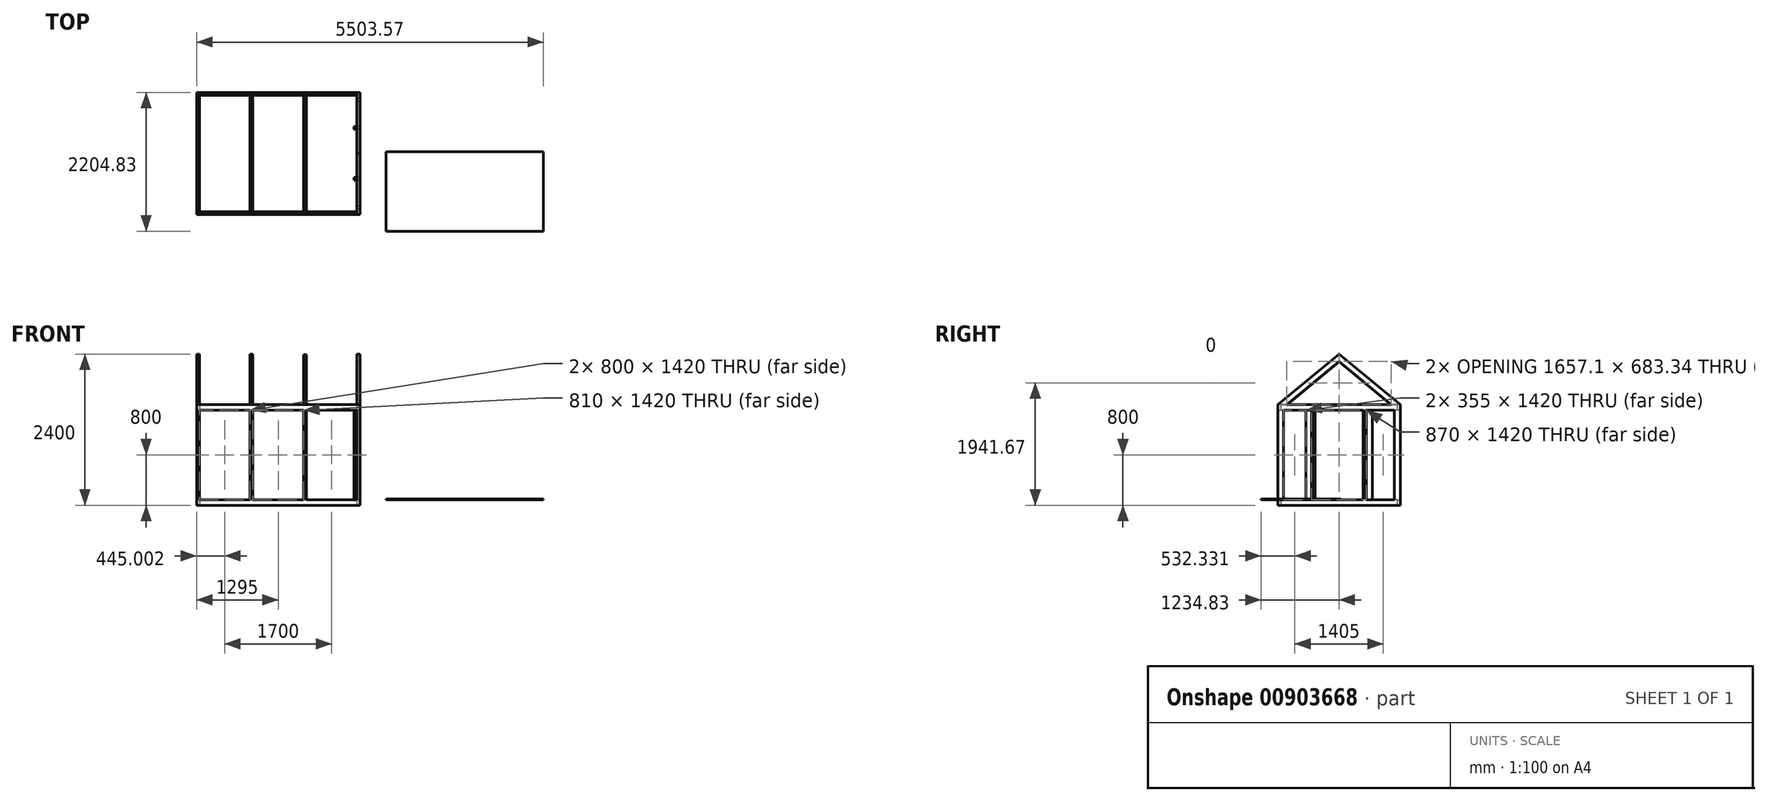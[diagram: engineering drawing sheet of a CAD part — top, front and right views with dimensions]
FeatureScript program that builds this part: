
annotation { "Feature Type Name" : "Feature", "Feature Type Description" : "" }
export const myFeature = defineFeature(function(context is Context, id is Id, definition is map)
    precondition{}
    {
        {
            var Q0;
            Q0=qCreatedBy(makeId("Top.planeOp"),FACE);
            var sketch = newSketch(context, id + "F0", { "sketchPlane" : qUnion([Q0])});
            skLineSegment(sketch, "E0.bottom", {"start": v(-727.48, 1617.18) * mm, "end": v(1862.52, 1617.18) * mm});
            skLineSegment(sketch, "E0.top", {"start": v(-727.48, -322.82) * mm, "end": v(1862.52, -322.82) * mm});
            skLineSegment(sketch, "E0.left", {"start": v(-727.48, 1617.18) * mm, "end": v(-727.48, -322.82) * mm});
            skLineSegment(sketch, "E0.right", {"start": v(1862.52, 1617.18) * mm, "end": v(1862.52, -322.82) * mm});
            skLineSegment(sketch, "E1.bottom", {"start": v(-682.48, 1572.18) * mm, "end": v(1817.52, 1572.18) * mm});
            skLineSegment(sketch, "E1.top", {"start": v(-682.48, -277.82) * mm, "end": v(1817.52, -277.82) * mm});
            skLineSegment(sketch, "E1.left", {"start": v(-682.48, 1572.18) * mm, "end": v(-682.48, -277.82) * mm});
            skLineSegment(sketch, "E1.right", {"start": v(1817.52, 1572.18) * mm, "end": v(1817.52, -277.82) * mm});
            skSolve(sketch);
        }
        {
            var Q0;
            Q0 = qSketchRegion(id + "F0", true);
            extrude(context, id + "F1", {"entities" : qUnion([Q0]), "depth" : 90 * mm, "offsetDistance" : 25 * mm});
        }
        {
            var Q0;
            Q0=makeQuery(id+"F1.opExtrude","CAP_FACE",FACE,{"disambiguationData":[OSD([sQuery(id+"F0.wireOp",EDGE,"E0.bottom"),sQuery(id+"F0.wireOp",EDGE,"E0.top"),sQuery(id+"F0.wireOp",EDGE,"E0.left"),sQuery(id+"F0.wireOp",EDGE,"E0.right"),sQuery(id+"F0.wireOp",EDGE,"E1.bottom"),sQuery(id+"F0.wireOp",EDGE,"E1.top"),sQuery(id+"F0.wireOp",EDGE,"E1.left"),sQuery(id+"F0.wireOp",EDGE,"E1.right")])],"isStart":false});
            var sketch = newSketch(context, id + "F2", { "sketchPlane" : qUnion([Q0])});
            skLineSegment(sketch, "E2.bottom", {"start": v(-727.48, -322.82) * mm, "end": v(-682.48, -322.82) * mm});
            skLineSegment(sketch, "E2.top", {"start": v(-727.48, -232.82) * mm, "end": v(-682.48, -232.82) * mm});
            skLineSegment(sketch, "E2.left", {"start": v(-727.48, -322.82) * mm, "end": v(-727.48, -232.82) * mm});
            skLineSegment(sketch, "E2.right", {"start": v(-682.48, -322.82) * mm, "end": v(-682.48, -232.82) * mm});
            skLineSegment(sketch, "E3.bottom", {"start": v(-727.48, 1617.18) * mm, "end": v(-682.48, 1617.18) * mm});
            skLineSegment(sketch, "E3.top", {"start": v(-727.48, 1527.18) * mm, "end": v(-682.48, 1527.18) * mm});
            skLineSegment(sketch, "E3.left", {"start": v(-727.48, 1617.18) * mm, "end": v(-727.48, 1527.18) * mm});
            skLineSegment(sketch, "E3.right", {"start": v(-682.48, 1617.18) * mm, "end": v(-682.48, 1527.18) * mm});
            skLineSegment(sketch, "E4.bottom", {"start": v(1862.52, 1617.18) * mm, "end": v(1817.52, 1617.18) * mm});
            skLineSegment(sketch, "E4.top", {"start": v(1862.52, 1527.18) * mm, "end": v(1817.52, 1527.18) * mm});
            skLineSegment(sketch, "E4.left", {"start": v(1862.52, 1617.18) * mm, "end": v(1862.52, 1527.18) * mm});
            skLineSegment(sketch, "E4.right", {"start": v(1817.52, 1617.18) * mm, "end": v(1817.52, 1527.18) * mm});
            skLineSegment(sketch, "E5.bottom", {"start": v(1862.52, -322.82) * mm, "end": v(1817.52, -322.82) * mm});
            skLineSegment(sketch, "E5.top", {"start": v(1862.52, -232.82) * mm, "end": v(1817.52, -232.82) * mm});
            skLineSegment(sketch, "E5.left", {"start": v(1862.52, -322.82) * mm, "end": v(1862.52, -232.82) * mm});
            skLineSegment(sketch, "E5.right", {"start": v(1817.52, -322.82) * mm, "end": v(1817.52, -232.82) * mm});
            skLineSegment(sketch, "E6.bottom", {"start": v(117.52, -232.82) * mm, "end": v(162.52, -232.82) * mm});
            skLineSegment(sketch, "E6.top", {"start": v(117.52, -322.82) * mm, "end": v(162.52, -322.82) * mm});
            skLineSegment(sketch, "E6.left", {"start": v(117.52, -232.82) * mm, "end": v(117.52, -322.82) * mm});
            skLineSegment(sketch, "E6.right", {"start": v(162.52, -232.82) * mm, "end": v(162.52, -322.82) * mm});
            skLineSegment(sketch, "E7.bottom", {"start": v(972.52, -232.82) * mm, "end": v(1017.52, -232.82) * mm});
            skLineSegment(sketch, "E7.top", {"start": v(972.52, -322.82) * mm, "end": v(1017.52, -322.82) * mm});
            skLineSegment(sketch, "E7.left", {"start": v(972.52, -232.82) * mm, "end": v(972.52, -322.82) * mm});
            skLineSegment(sketch, "E7.right", {"start": v(1017.52, -232.82) * mm, "end": v(1017.52, -322.82) * mm});
            skLineSegment(sketch, "E8.bottom", {"start": v(117.52, 1617.18) * mm, "end": v(162.52, 1617.18) * mm});
            skLineSegment(sketch, "E8.top", {"start": v(117.52, 1527.18) * mm, "end": v(162.52, 1527.18) * mm});
            skLineSegment(sketch, "E8.left", {"start": v(117.52, 1617.18) * mm, "end": v(117.52, 1527.18) * mm});
            skLineSegment(sketch, "E8.right", {"start": v(162.52, 1617.18) * mm, "end": v(162.52, 1527.18) * mm});
            skLineSegment(sketch, "E9.bottom", {"start": v(1017.52, 1527.18) * mm, "end": v(972.52, 1527.18) * mm});
            skLineSegment(sketch, "E9.top", {"start": v(1017.52, 1617.18) * mm, "end": v(972.52, 1617.18) * mm});
            skLineSegment(sketch, "E9.left", {"start": v(1017.52, 1527.18) * mm, "end": v(1017.52, 1617.18) * mm});
            skLineSegment(sketch, "E9.right", {"start": v(972.52, 1527.18) * mm, "end": v(972.52, 1617.18) * mm});
            skLineSegment(sketch, "E10.bottom", {"start": v(-727.48, 1172.18) * mm, "end": v(-682.48, 1172.18) * mm});
            skLineSegment(sketch, "E10.top", {"start": v(-727.48, 1082.18) * mm, "end": v(-682.48, 1082.18) * mm});
            skLineSegment(sketch, "E10.left", {"start": v(-727.48, 1172.18) * mm, "end": v(-727.48, 1082.18) * mm});
            skLineSegment(sketch, "E10.right", {"start": v(-682.48, 1172.18) * mm, "end": v(-682.48, 1082.18) * mm});
            skLineSegment(sketch, "E11.bottom", {"start": v(-727.48, 212.18) * mm, "end": v(-682.48, 212.18) * mm});
            skLineSegment(sketch, "E11.top", {"start": v(-727.48, 122.18) * mm, "end": v(-682.48, 122.18) * mm});
            skLineSegment(sketch, "E11.left", {"start": v(-727.48, 212.18) * mm, "end": v(-727.48, 122.18) * mm});
            skLineSegment(sketch, "E11.right", {"start": v(-682.48, 212.18) * mm, "end": v(-682.48, 122.18) * mm});
            skLineSegment(sketch, "E12.bottom", {"start": v(1862.52, 1072.18) * mm, "end": v(1772.52, 1072.18) * mm});
            skLineSegment(sketch, "E12.top", {"start": v(1862.52, 1027.18) * mm, "end": v(1772.52, 1027.18) * mm});
            skLineSegment(sketch, "E12.left", {"start": v(1862.52, 1072.18) * mm, "end": v(1862.52, 1027.18) * mm});
            skLineSegment(sketch, "E12.right", {"start": v(1772.52, 1072.18) * mm, "end": v(1772.52, 1027.18) * mm});
            skLineSegment(sketch, "E13.bottom", {"start": v(1862.52, 267.18) * mm, "end": v(1772.52, 267.18) * mm});
            skLineSegment(sketch, "E13.top", {"start": v(1862.52, 222.18) * mm, "end": v(1772.52, 222.18) * mm});
            skLineSegment(sketch, "E13.left", {"start": v(1862.52, 267.18) * mm, "end": v(1862.52, 222.18) * mm});
            skLineSegment(sketch, "E13.right", {"start": v(1772.52, 267.18) * mm, "end": v(1772.52, 222.18) * mm});
            skSolve(sketch);
        }
        {
            var Q0;
            {var subQ0=sQuery(id+"F2.wireOp",EDGE,"E10.left");Q0=makeQuery(id+"F2.imprint","IMPRINT",FACE,{"disambiguationData":[TD([[makeQuery(id+"F2.imprint","IMPRINT",EDGE,{"derivedFrom":subQ0}),1.0]])]});}
            var Q1;
            {var subQ0=sQuery(id+"F2.wireOp",EDGE,"E10.right");Q1=makeQuery(id+"F2.imprint","IMPRINT",FACE,{"disambiguationData":[TD([[makeQuery(id+"F2.imprint","IMPRINT",EDGE,{"derivedFrom":subQ0}),-1.0]])]});}
            var Q2;
            {var subQ0=sQuery(id+"F2.wireOp",EDGE,"E11.left");Q2=makeQuery(id+"F2.imprint","IMPRINT",FACE,{"disambiguationData":[TD([[makeQuery(id+"F2.imprint","IMPRINT",EDGE,{"derivedFrom":subQ0}),1.0]])]});}
            var Q3;
            {var subQ0=sQuery(id+"F2.wireOp",EDGE,"E11.right");Q3=makeQuery(id+"F2.imprint","IMPRINT",FACE,{"disambiguationData":[TD([[makeQuery(id+"F2.imprint","IMPRINT",EDGE,{"derivedFrom":subQ0}),-1.0]])]});}
            var Q4;
            {var subQ2=sQuery(id+"F2.wireOp",EDGE,"E2.bottom");Q4=makeQuery(id+"F2.imprint","IMPRINT",FACE,{"disambiguationData":[TD([[makeQuery(id+"F2.imprint","IMPRINT",EDGE,{"derivedFrom":subQ2}),1.0]])]});}
            var Q5;
            {var subQ0=sQuery(id+"F2.wireOp",EDGE,"E6.bottom");Q5=makeQuery(id+"F2.imprint","IMPRINT",FACE,{"disambiguationData":[TD([[makeQuery(id+"F2.imprint","IMPRINT",EDGE,{"derivedFrom":subQ0}),-1.0]])]});}
            var Q6;
            {var subQ0=sQuery(id+"F2.wireOp",EDGE,"E6.top");Q6=makeQuery(id+"F2.imprint","IMPRINT",FACE,{"disambiguationData":[TD([[makeQuery(id+"F2.imprint","IMPRINT",EDGE,{"derivedFrom":subQ0}),1.0]])]});}
            var Q7;
            {var subQ0=sQuery(id+"F2.wireOp",EDGE,"E7.bottom");Q7=makeQuery(id+"F2.imprint","IMPRINT",FACE,{"disambiguationData":[TD([[makeQuery(id+"F2.imprint","IMPRINT",EDGE,{"derivedFrom":subQ0}),-1.0]])]});}
            var Q8;
            {var subQ0=sQuery(id+"F2.wireOp",EDGE,"E7.top");Q8=makeQuery(id+"F2.imprint","IMPRINT",FACE,{"disambiguationData":[TD([[makeQuery(id+"F2.imprint","IMPRINT",EDGE,{"derivedFrom":subQ0}),1.0]])]});}
            var Q9;
            {var subQ2=sQuery(id+"F2.wireOp",EDGE,"E5.bottom");Q9=makeQuery(id+"F2.imprint","IMPRINT",FACE,{"disambiguationData":[TD([[makeQuery(id+"F2.imprint","IMPRINT",EDGE,{"derivedFrom":subQ2}),1.0]])]});}
            var Q10;
            {var subQ0=sQuery(id+"F2.wireOp",EDGE,"E13.right");Q10=makeQuery(id+"F2.imprint","IMPRINT",FACE,{"disambiguationData":[TD([[makeQuery(id+"F2.imprint","IMPRINT",EDGE,{"derivedFrom":subQ0}),1.0]])]});}
            var Q11;
            {var subQ0=sQuery(id+"F2.wireOp",EDGE,"E13.left");Q11=makeQuery(id+"F2.imprint","IMPRINT",FACE,{"disambiguationData":[TD([[makeQuery(id+"F2.imprint","IMPRINT",EDGE,{"derivedFrom":subQ0}),-1.0]])]});}
            var Q12;
            {var subQ0=sQuery(id+"F2.wireOp",EDGE,"E12.right");Q12=makeQuery(id+"F2.imprint","IMPRINT",FACE,{"disambiguationData":[TD([[makeQuery(id+"F2.imprint","IMPRINT",EDGE,{"derivedFrom":subQ0}),1.0]])]});}
            var Q13;
            {var subQ0=sQuery(id+"F2.wireOp",EDGE,"E12.left");Q13=makeQuery(id+"F2.imprint","IMPRINT",FACE,{"disambiguationData":[TD([[makeQuery(id+"F2.imprint","IMPRINT",EDGE,{"derivedFrom":subQ0}),-1.0]])]});}
            var Q14;
            {var subQ3=sQuery(id+"F2.wireOp",EDGE,"E4.bottom");Q14=makeQuery(id+"F2.imprint","IMPRINT",FACE,{"disambiguationData":[TD([[makeQuery(id+"F2.imprint","IMPRINT",EDGE,{"derivedFrom":subQ3}),-1.0]])]});}
            var Q15;
            {var subQ0=sQuery(id+"F2.wireOp",EDGE,"E9.top");Q15=makeQuery(id+"F2.imprint","IMPRINT",FACE,{"disambiguationData":[TD([[makeQuery(id+"F2.imprint","IMPRINT",EDGE,{"derivedFrom":subQ0}),-1.0]])]});}
            var Q16;
            {var subQ0=sQuery(id+"F2.wireOp",EDGE,"E9.bottom");Q16=makeQuery(id+"F2.imprint","IMPRINT",FACE,{"disambiguationData":[TD([[makeQuery(id+"F2.imprint","IMPRINT",EDGE,{"derivedFrom":subQ0}),-1.0]])]});}
            var Q17;
            {var subQ0=sQuery(id+"F2.wireOp",EDGE,"E8.bottom");Q17=makeQuery(id+"F2.imprint","IMPRINT",FACE,{"disambiguationData":[TD([[makeQuery(id+"F2.imprint","IMPRINT",EDGE,{"derivedFrom":subQ0}),-1.0]])]});}
            var Q18;
            {var subQ0=sQuery(id+"F2.wireOp",EDGE,"E8.top");Q18=makeQuery(id+"F2.imprint","IMPRINT",FACE,{"disambiguationData":[TD([[makeQuery(id+"F2.imprint","IMPRINT",EDGE,{"derivedFrom":subQ0}),1.0]])]});}
            var Q19;
            {var subQ3=sQuery(id+"F2.wireOp",EDGE,"E3.bottom");Q19=makeQuery(id+"F2.imprint","IMPRINT",FACE,{"disambiguationData":[TD([[makeQuery(id+"F2.imprint","IMPRINT",EDGE,{"derivedFrom":subQ3}),-1.0]])]});}
            extrude(context, id + "F3", {"entities" : qUnion([Q0, Q1, Q2, Q3, Q4, Q5, Q6, Q7, Q8, Q9, Q10, Q11, Q12, Q13, Q14, Q15, Q16, Q17, Q18, Q19]), "operationType" : NewBodyOperationType.ADD, "depth" : 1420 * mm, "offsetDistance" : 25 * mm});
        }
        {
            var Q0;
            Q0=makeQuery(id+"F3.opExtrude","CAP_FACE",FACE,{"disambiguationData":[OSD([sQuery(id+"F2.wireOp",EDGE,"E3.bottom"),sQuery(id+"F2.wireOp",EDGE,"E3.top"),sQuery(id+"F2.wireOp",EDGE,"E3.left"),sQuery(id+"F2.wireOp",EDGE,"E3.right")])],"isStart":false});
            var sketch = newSketch(context, id + "F4", { "sketchPlane" : qUnion([Q0])});
            skLineSegment(sketch, "E14.bottom", {"start": v(-727.48, 1617.18) * mm, "end": v(1862.52, 1617.18) * mm});
            skLineSegment(sketch, "E14.top", {"start": v(-727.48, -322.82) * mm, "end": v(1862.52, -322.82) * mm});
            skLineSegment(sketch, "E14.left", {"start": v(-727.48, 1617.18) * mm, "end": v(-727.48, -322.82) * mm});
            skLineSegment(sketch, "E14.right", {"start": v(1862.52, 1617.18) * mm, "end": v(1862.52, -322.82) * mm});
            skLineSegment(sketch, "E15.bottom", {"start": v(-682.48, 1572.18) * mm, "end": v(1817.52, 1572.18) * mm});
            skLineSegment(sketch, "E15.top", {"start": v(-682.48, -277.82) * mm, "end": v(1817.52, -277.82) * mm});
            skLineSegment(sketch, "E15.left", {"start": v(-682.48, 1572.18) * mm, "end": v(-682.48, -277.82) * mm});
            skLineSegment(sketch, "E15.right", {"start": v(1817.52, 1572.18) * mm, "end": v(1817.52, -277.82) * mm});
            skSolve(sketch);
        }
        {
            var Q0;
            Q0 = qSketchRegion(id + "F4", true);
            extrude(context, id + "F5", {"entities" : qUnion([Q0]), "operationType" : NewBodyOperationType.ADD, "depth" : 90 * mm, "offsetDistance" : 25 * mm});
        }
        {
            var Q0;
            Q0=makeQuery(id+"F5.boolean.opBoolean","MERGE",FACE,{"derivedFrom":[makeQuery(id+"F3.boolean.opBoolean","MERGE",FACE,{"derivedFrom":[makeQuery(id+"F1.opExtrude","SWEPT_FACE",FACE,{"disambiguationData":[OSD([sQuery(id+"F0.wireOp",EDGE,"E0.right")])]}),makeQuery(id+"F3.opExtrude","SWEPT_FACE",FACE,{"disambiguationData":[OSD([sQuery(id+"F2.wireOp",EDGE,"E4.left")])]}),makeQuery(id+"F3.opExtrude","SWEPT_FACE",FACE,{"disambiguationData":[OSD([sQuery(id+"F2.wireOp",EDGE,"E5.left")])]}),makeQuery(id+"F3.opExtrude","SWEPT_FACE",FACE,{"disambiguationData":[OSD([sQuery(id+"F2.wireOp",EDGE,"E12.left")])]}),makeQuery(id+"F3.opExtrude","SWEPT_FACE",FACE,{"disambiguationData":[OSD([sQuery(id+"F2.wireOp",EDGE,"E13.left")])]})]}),makeQuery(id+"F5.opExtrude","SWEPT_FACE",FACE,{"disambiguationData":[OSD([sQuery(id+"F4.wireOp",EDGE,"E14.right")])]})]});
            var sketch = newSketch(context, id + "F6", { "sketchPlane" : qUnion([Q0])});
            skLineSegment(sketch, "E16.bottom", {"start": v(-322.82, 1600) * mm, "end": v(1617.18, 1600) * mm});
            skLineSegment(sketch, "E16.top", {"start": v(-322.82, 2400) * mm, "end": v(1617.18, 2400) * mm});
            skLineSegment(sketch, "E16.left", {"start": v(-322.82, 1600) * mm, "end": v(-322.82, 2400) * mm});
            skLineSegment(sketch, "E16.right", {"start": v(1617.18, 1600) * mm, "end": v(1617.18, 2400) * mm});
            skPoint(sketch, "E17", {"position": v(647.18, 2400) * mm});
            skLineSegment(sketch, "E18", {"start": v(-322.82, 1600) * mm, "end": v(647.18, 2400) * mm});
            skLineSegment(sketch, "E19", {"start": v(647.18, 2400) * mm, "end": v(1617.18, 1600) * mm});
            skLineSegment(sketch, "E20", {"start": v(647.18, 2283.34) * mm, "end": v(-181.37, 1600) * mm});
            skLineSegment(sketch, "E21", {"start": v(647.18, 2283.34) * mm, "end": v(1475.73, 1600) * mm});
            skSolve(sketch);
        }
        {
            var Q0;
            {var subQ1=sQuery(id+"F6.wireOp",EDGE,"E18");Q0=makeQuery(id+"F6.imprint","IMPRINT",FACE,{"disambiguationData":[TD([[makeQuery(id+"F6.imprint","IMPRINT",EDGE,{"derivedFrom":subQ1}),-1.0]])]});}
            extrude(context, id + "F7", {"entities" : qUnion([Q0]), "operationType" : NewBodyOperationType.ADD, "oppositeDirection" : true, "depth" : 45 * mm, "offsetDistance" : 25 * mm});
        }
        {
            var Q0;
            Q0=makeQuery(id+"F3.opExtrude","SWEPT_FACE",FACE,{"disambiguationData":[OSD([sQuery(id+"F2.wireOp",EDGE,"E9.right")])]});
            var sketch = newSketch(context, id + "F8", { "sketchPlane" : qUnion([Q0])});
            skLineSegment(sketch, "E22.bottom", {"start": v(-1617.18, 1593.4) * mm, "end": v(322.82, 1593.4) * mm});
            skLineSegment(sketch, "E22.top", {"start": v(-1617.18, 2393.4) * mm, "end": v(322.82, 2393.4) * mm});
            skLineSegment(sketch, "E22.left", {"start": v(-1617.18, 1593.4) * mm, "end": v(-1617.18, 2393.4) * mm});
            skLineSegment(sketch, "E22.right", {"start": v(322.82, 1593.4) * mm, "end": v(322.82, 2393.4) * mm});
            skPoint(sketch, "E23", {"position": v(-647.18, 2393.4) * mm});
            skLineSegment(sketch, "E24", {"start": v(-1617.18, 1593.4) * mm, "end": v(-647.18, 2393.4) * mm});
            skLineSegment(sketch, "E25", {"start": v(-647.18, 2393.4) * mm, "end": v(322.82, 1593.4) * mm});
            skLineSegment(sketch, "E26", {"start": v(-647.18, 2276.74) * mm, "end": v(-1475.73, 1593.4) * mm});
            skLineSegment(sketch, "E27", {"start": v(-647.18, 2276.74) * mm, "end": v(181.37, 1593.4) * mm});
            skSolve(sketch);
        }
        {
            var Q0;
            {var subQ1=sQuery(id+"F8.wireOp",EDGE,"E24");Q0=makeQuery(id+"F8.imprint","IMPRINT",FACE,{"disambiguationData":[TD([[makeQuery(id+"F8.imprint","IMPRINT",EDGE,{"derivedFrom":subQ1}),-1.0]])]});}
            extrude(context, id + "F9", {"entities" : qUnion([Q0]), "operationType" : NewBodyOperationType.ADD, "oppositeDirection" : true, "depth" : 45 * mm, "offsetDistance" : 25 * mm});
        }
        {
            var Q0;
            Q0=makeQuery(id+"F3.opExtrude","SWEPT_FACE",FACE,{"disambiguationData":[OSD([sQuery(id+"F2.wireOp",EDGE,"E8.left")])]});
            var sketch = newSketch(context, id + "F10", { "sketchPlane" : qUnion([Q0])});
            skLineSegment(sketch, "E28.bottom", {"start": v(-1617.18, 1600) * mm, "end": v(322.82, 1600) * mm});
            skLineSegment(sketch, "E28.top", {"start": v(-1617.18, 2400) * mm, "end": v(322.82, 2400) * mm});
            skLineSegment(sketch, "E28.left", {"start": v(-1617.18, 1600) * mm, "end": v(-1617.18, 2400) * mm});
            skLineSegment(sketch, "E28.right", {"start": v(322.82, 1600) * mm, "end": v(322.82, 2400) * mm});
            skPoint(sketch, "E29", {"position": v(-647.18, 2400) * mm});
            skLineSegment(sketch, "E30", {"start": v(-1617.18, 1600) * mm, "end": v(-647.18, 2400) * mm});
            skLineSegment(sketch, "E31", {"start": v(-647.18, 2400) * mm, "end": v(322.82, 1600) * mm});
            skLineSegment(sketch, "E32", {"start": v(-647.18, 2283.34) * mm, "end": v(-1475.73, 1600) * mm});
            skLineSegment(sketch, "E33", {"start": v(-647.18, 2283.34) * mm, "end": v(181.37, 1600) * mm});
            skSolve(sketch);
        }
        {
            var Q0;
            {var subQ1=sQuery(id+"F10.wireOp",EDGE,"E30");Q0=makeQuery(id+"F10.imprint","IMPRINT",FACE,{"disambiguationData":[TD([[makeQuery(id+"F10.imprint","IMPRINT",EDGE,{"derivedFrom":subQ1}),-1.0]])]});}
            extrude(context, id + "F11", {"entities" : qUnion([Q0]), "operationType" : NewBodyOperationType.ADD, "oppositeDirection" : true, "depth" : 45 * mm, "offsetDistance" : 25 * mm});
        }
        {
            var Q0;
            Q0=makeQuery(id+"F5.boolean.opBoolean","MERGE",FACE,{"derivedFrom":[makeQuery(id+"F3.boolean.opBoolean","MERGE",FACE,{"derivedFrom":[makeQuery(id+"F1.opExtrude","SWEPT_FACE",FACE,{"disambiguationData":[OSD([sQuery(id+"F0.wireOp",EDGE,"E0.left")])]}),makeQuery(id+"F3.opExtrude","SWEPT_FACE",FACE,{"disambiguationData":[OSD([sQuery(id+"F2.wireOp",EDGE,"E2.left")])]}),makeQuery(id+"F3.opExtrude","SWEPT_FACE",FACE,{"disambiguationData":[OSD([sQuery(id+"F2.wireOp",EDGE,"E3.left")])]}),makeQuery(id+"F3.opExtrude","SWEPT_FACE",FACE,{"disambiguationData":[OSD([sQuery(id+"F2.wireOp",EDGE,"E10.left")])]}),makeQuery(id+"F3.opExtrude","SWEPT_FACE",FACE,{"disambiguationData":[OSD([sQuery(id+"F2.wireOp",EDGE,"E11.left")])]})]}),makeQuery(id+"F5.opExtrude","SWEPT_FACE",FACE,{"disambiguationData":[OSD([sQuery(id+"F4.wireOp",EDGE,"E14.left")])]})]});
            var sketch = newSketch(context, id + "F12", { "sketchPlane" : qUnion([Q0])});
            skLineSegment(sketch, "E34.bottom", {"start": v(-1617.18, 1600) * mm, "end": v(322.82, 1600) * mm});
            skLineSegment(sketch, "E34.top", {"start": v(-1617.18, 2400) * mm, "end": v(322.82, 2400) * mm});
            skLineSegment(sketch, "E34.left", {"start": v(-1617.18, 1600) * mm, "end": v(-1617.18, 2400) * mm});
            skLineSegment(sketch, "E34.right", {"start": v(322.82, 1600) * mm, "end": v(322.82, 2400) * mm});
            skPoint(sketch, "E35", {"position": v(-647.18, 2400) * mm});
            skLineSegment(sketch, "E36", {"start": v(-1617.18, 1600) * mm, "end": v(-647.18, 2400) * mm});
            skLineSegment(sketch, "E37", {"start": v(-647.18, 2400) * mm, "end": v(322.82, 1600) * mm});
            skLineSegment(sketch, "E38", {"start": v(-647.18, 2283.34) * mm, "end": v(-1475.73, 1600) * mm});
            skLineSegment(sketch, "E39", {"start": v(-647.18, 2283.34) * mm, "end": v(181.37, 1600) * mm});
            skSolve(sketch);
        }
        {
            var Q0;
            {var subQ1=sQuery(id+"F12.wireOp",EDGE,"E36");Q0=makeQuery(id+"F12.imprint","IMPRINT",FACE,{"disambiguationData":[TD([[makeQuery(id+"F12.imprint","IMPRINT",EDGE,{"derivedFrom":subQ1}),-1.0]])]});}
            extrude(context, id + "F13", {"entities" : qUnion([Q0]), "operationType" : NewBodyOperationType.ADD, "oppositeDirection" : true, "depth" : 45 * mm, "offsetDistance" : 25 * mm});
        }
        {
            var Q0;
            {var subQ32=sQuery(id+"F2.wireOp",EDGE,"E6.bottom");Q0=makeQuery(id+"F2.imprint","IMPRINT",FACE,{"disambiguationData":[TD([[makeQuery(id+"F2.imprint","IMPRINT",EDGE,{"derivedFrom":subQ32}),1.0]])]});}
            var sketch = newSketch(context, id + "F14", { "sketchPlane" : qUnion([Q0])});
            skLineSegment(sketch, "E40.bottom", {"start": v(2276.1, 672.35) * mm, "end": v(4776.1, 672.35) * mm});
            skLineSegment(sketch, "E40.top", {"start": v(2276.1, -587.65) * mm, "end": v(4776.1, -587.65) * mm});
            skLineSegment(sketch, "E40.left", {"start": v(2276.1, 672.35) * mm, "end": v(2276.1, -587.65) * mm});
            skLineSegment(sketch, "E40.right", {"start": v(4776.1, 672.35) * mm, "end": v(4776.1, -587.65) * mm});
            skSolve(sketch);
        }
        {
            var Q0;
            Q0=makeQuery(id+"F14.imprint","IMPRINT",FACE,{"disambiguationData":[TD([[makeQuery(id+"F14.imprint","IMPRINT",EDGE,{"derivedFrom":sQuery(id+"F14.wireOp",EDGE,"E40.bottom")}),-1.0]])]});
            extrude(context, id + "F15", {"entities" : qUnion([Q0]), "depth" : 10 * mm, "offsetDistance" : 25 * mm});
        }
    });
